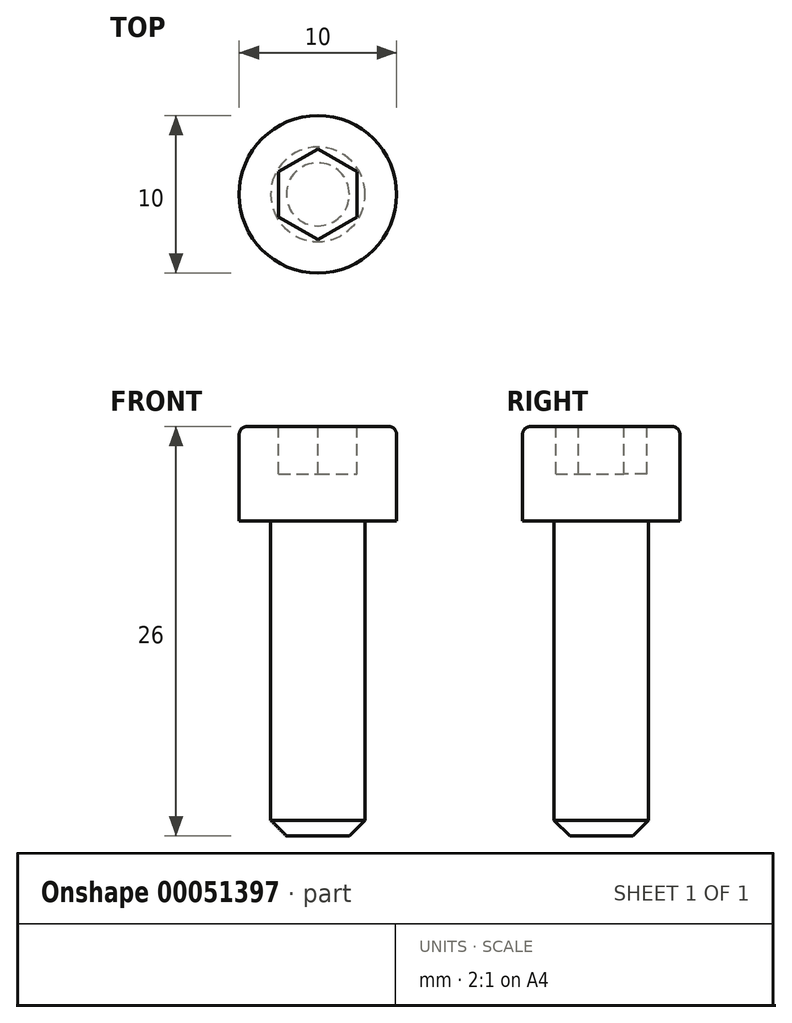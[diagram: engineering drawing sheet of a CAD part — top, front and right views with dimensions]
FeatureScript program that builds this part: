
annotation { "Feature Type Name" : "Feature", "Feature Type Description" : "" }
export const myFeature = defineFeature(function(context is Context, id is Id, definition is map)
    precondition{}
    {
        {
            var Q0;
            Q0=qCreatedBy(makeId("Top.planeOp"),FACE);
            var sketch = newSketch(context, id + "F0", { "sketchPlane" : qUnion([Q0])});
            skCircle(sketch, "E0", {"center": v(0, 0) * mm, "radius": 5 * mm});
            skSolve(sketch);
        }
        {
            var Q0;
            Q0=makeQuery(id+"F0.imprint","IMPRINT",FACE,{"disambiguationData":[TD([[makeQuery(id+"F0.imprint","IMPRINT",EDGE,{"derivedFrom":sQuery(id+"F0.wireOp",EDGE,"E0")}),1.0]])]});
            extrude(context, id + "F1", {"entities" : qUnion([Q0]), "depth" : 6 * mm});
        }
        {
            var Q0;
            Q0=makeQuery(id+"F1.opExtrude","CAP_EDGE",EDGE,{"disambiguationData":[OSD([sQuery(id+"F0.wireOp",EDGE,"E0")])],"isStart":false});
            fillet(context, id + "F2", {"entities" : qUnion([Q0]), "radius" : 0.5 * mm, "tangentPropagation" : true, "allowEdgeOverflow" : false});
        }
        {
            var Q0;
            Q0=makeQuery(id+"F1.opExtrude","CAP_FACE",FACE,{"disambiguationData":[OSD([sQuery(id+"F0.wireOp",EDGE,"E0")])],"isStart":false});
            var sketch = newSketch(context, id + "F3", { "sketchPlane" : qUnion([Q0])});
            skCircle(sketch, "E1.cCircle", {"center": v(0, 0) * mm, "radius": 2.5 * mm, "construction": true});
            skLineSegment(sketch, "E1.0", {"start": v(0, 2.89) * mm, "end": v(2.5, 1.44) * mm});
            skLineSegment(sketch, "E1.1", {"start": v(2.5, 1.44) * mm, "end": v(2.5, -1.44) * mm});
            skLineSegment(sketch, "E1.2", {"start": v(2.5, -1.44) * mm, "end": v(0, -2.89) * mm});
            skLineSegment(sketch, "E1.3", {"start": v(0, -2.89) * mm, "end": v(-2.5, -1.44) * mm});
            skLineSegment(sketch, "E1.4", {"start": v(-2.5, -1.44) * mm, "end": v(-2.5, 1.44) * mm});
            skLineSegment(sketch, "E1.5", {"start": v(-2.5, 1.44) * mm, "end": v(0, 2.89) * mm});
            skPoint(sketch, "E1.0.midPoint", {"position": v(1.25, 2.17) * mm});
            skSolve(sketch);
        }
        {
            var Q0;
            Q0 = qSketchRegion(id + "F3", true);
            extrude(context, id + "F4", {"entities" : qUnion([Q0]), "operationType" : NewBodyOperationType.REMOVE, "oppositeDirection" : true, "depth" : 3 * mm});
        }
        {
            var Q0;
            Q0=makeQuery(id+"F1.opExtrude","CAP_FACE",FACE,{"disambiguationData":[OSD([sQuery(id+"F0.wireOp",EDGE,"E0")])],"isStart":true});
            var sketch = newSketch(context, id + "F5", { "sketchPlane" : qUnion([Q0])});
            skCircle(sketch, "E2", {"center": v(0, 0) * mm, "radius": 3 * mm});
            skSolve(sketch);
        }
        {
            var Q0;
            Q0 = qSketchRegion(id + "F5", true);
            extrude(context, id + "F6", {"entities" : qUnion([Q0]), "operationType" : NewBodyOperationType.ADD, "depth" : 20 * mm});
        }
        {
            var Q0;
            Q0=makeQuery(id+"F6.opExtrude","CAP_EDGE",EDGE,{"disambiguationData":[OSD([sQuery(id+"F5.wireOp",EDGE,"E2")])],"isStart":false});
            chamfer(context, id + "F7", {"entities" : qUnion([Q0]), "width" : 1 * mm, "tangentPropagation" : true});
        }
    });
